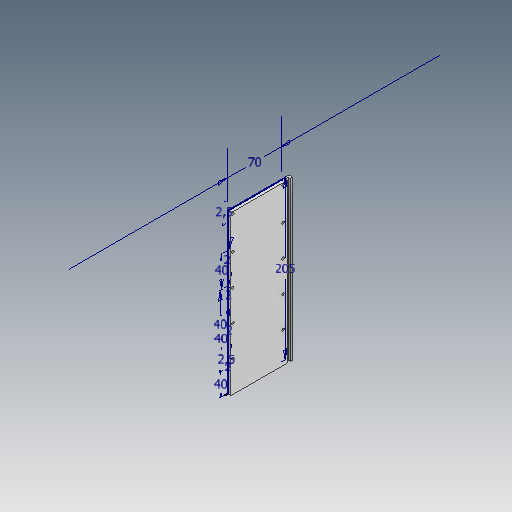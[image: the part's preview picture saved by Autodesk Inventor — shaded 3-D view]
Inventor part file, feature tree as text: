
AUTODESK INVENTOR PART (.ipt)
format: ipt  version: 2020.3 (Build 243373010, 373A)  size: 137,216 bytes
history: native  units: mm
features: sketch x3, extrude x3, hole x1
ambient origin geometry x8: Origin, YZ Plane, XZ Plane, XY Plane, X Axis, Y Axis, Z Axis, Center Point
bodies: Solid1 (feature_tree)
feature tree (7):
  sketch  "Sketch1"  dims[d0=205.0mm d1=70.0mm]
  extrude  "Extrusion1"  Depth=205.0mm
  hole  "Hole1"  [1 undecoded]
  extrude  "Extrusion2"  Depth=5.0mm TaperAngle=0.0deg
  extrude  "Extrusion3"  Depth=10.0mm TaperAngle=0.0deg
  sketch  "Sketch2"  dims[d2=2.0mm d3=2.0mm d4=2.0mm d5=2.0mm d7=40.0mm d8=40.0mm d9=40.0mm d10=2.5mm d11=40.0mm]
  sketch  "Sketch3"  dims[d12=2.5mm d13=5.0mm d14=0.0mm d15=3.242mm d16=8.0mm d17=4.0mm d18=2.0mm d19=90.0deg d20=11.8mm d21=0.0mm d22=10.0mm d23=0.0mm d24=10.0mm d25=2.5mm d26=4.0mm d27=3.0mm d28=10.0mm d29=0.0mm]
note: 1 required parameter value undecoded (feature->parameter linkage not recoverable at this tier; creation-order binding heuristic only, values carry confidence <= 0.55)
